# Revit family: Shower-Shower_Column_Kit-KOHLER-Aleo-K-26241T.rfa_
name_source: partatom
category: Plumbing Fixtures
units: mm (PartAtom-declared; Revit-internal decimal feet)

## family parameters
Cut with Voids When Loaded = No
Host = Face
Maintain Annotation Orientation = No
OmniClass Number = 23.31.17.00
OmniClass Title = Showers
Part Type = Normal
Room Calculation Point = No
Round Connector Dimension = Use Diameter
Shared = No

## types (4) — shared parameters
ADA Compliant = No
Assembly Code = D2010700
CW Connection = Yes
Cold Water Inlet = Cold Water Inlet
Date Modified = 10/11/2023
Default Elevation = 36"
HW Connection = Yes
Handle Clearance = 3 5/8"
Height = 51 1/8"
Hot Water Inlet = Hot Water Inlet
Manufacturer = Kohler Co.
Master Format 2014 = 22 42 23
Master Format 2014 Name = Residential Showers
Material = Premium Metal Construction
Product Documentation Link = https://files.kohler.com.cn
Product Name = Aleo
Product Page URL = https://www.kohler.com.cn
URL = http://www.kohler.com.cn
Vent Connection = No
Waste Connection = No
Waste Water Outlet = Waste Water Outlet
WaterSense Certified = No
Width = 5 7/8"

## per-type parameters (varying)
| type | 4 | B4 | Description | Finish | Flow Rate | Length | Model | Pressure | Secondary Finish | Type |
| 4, CP-Polished Chrome | Yes | No | Leo Double Rain Shower Column Rigid Tube Connection (Round Head) | Kohler-Metal-CP-Polished_Chrome | 0 GPM | 24 1/4" | K-26241T-4-CP | 0.00 psi | Kohler-Plastic-0-White | 2 |
| 4, BL-Matte Black | Yes | No | Leo Double Rain Shower Column Rigid Tube Connection (Round Head) | Kohler-Metal-BL-Matte_Black | 0 GPM | 24 1/4" | K-26241T-4-BL | 0.00 psi | Plastic-Pantone-PQ-194205-TCX | 1 |
| B4, BL-Matte Black | No | Yes | Leo Three Outlet Shower Column Rigid Pipe Connection (Round Overhead) | Kohler-Metal-BL-Matte_Black | 8 GPM | 25 1/4" | K-26241T-B4-BL | 60.00 psi | Plastic-Pantone-PQ-194205-TCX | 3 |
| B4, CP-Polished Chrome | No | Yes | Leo Three Outlet Shower Column Rigid Pipe Connection (Round Overhead) | Kohler-Metal-CP-Polished_Chrome | 8 GPM | 25 1/4" | K-26241T-B4-CP | 60.00 psi | Kohler-Plastic-0-White | 4 |

## geometry (parser evidence)
native form markers: Sweep x8
no freeform markers — native parametric forms only
